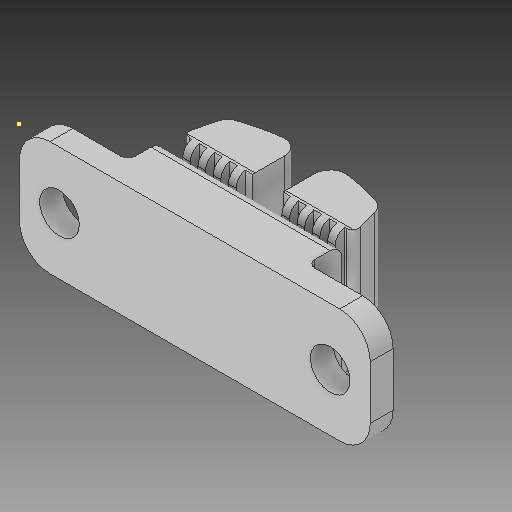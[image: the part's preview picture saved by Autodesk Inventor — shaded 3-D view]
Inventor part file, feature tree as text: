
AUTODESK INVENTOR PART (.ipt)
format: ipt  version: 2018 (Build 220112000, 112)  size: 298,496 bytes
history: native  units: mm
features: sketch x12, other x3
ambient origin geometry x8: Origin, YZ Plane, XZ Plane, XY Plane, X Axis, Y Axis, Z Axis, Center Point
bodies: Solid1 (feature_tree)
feature tree (15):
  other  "X Belt Clamp.ipt"
  other  "Solid1::X Belt Clamp.ipt"
  other  "TaggingFeature1"
  sketch  "Sketch1"  dims[d0=10.0mm]
  sketch  "Sketch2"
  sketch  "Sketch3"
  sketch  "Sketch4"
  sketch  "Sketch5"
  sketch  "Sketch6"
  sketch  "Sketch7"
  sketch  "Sketch8"
  sketch  "Sketch9"
  sketch  "Sketch10"
  sketch  "Sketch11"
  sketch  "Sketch12"
